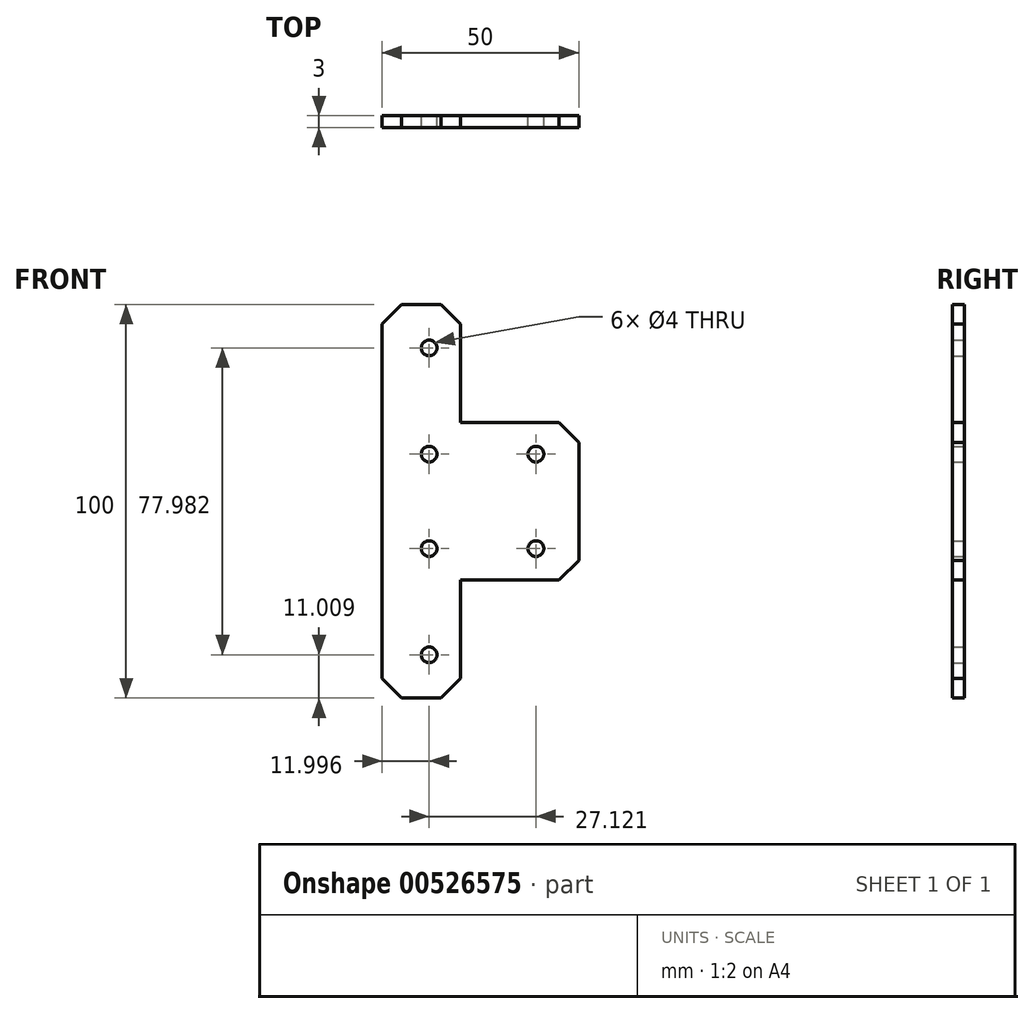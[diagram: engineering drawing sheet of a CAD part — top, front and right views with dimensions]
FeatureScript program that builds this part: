
annotation { "Feature Type Name" : "Feature", "Feature Type Description" : "" }
export const myFeature = defineFeature(function(context is Context, id is Id, definition is map)
    precondition{}
    {
        {
            var Q0;
            Q0=qCreatedBy(makeId("Front.planeOp"),FACE);
            var sketch = newSketch(context, id + "F0", { "sketchPlane" : qUnion([Q0])});
            skLineSegment(sketch, "E0", {"start": v(-55.77, 50) * mm, "end": v(-55.77, 0) * mm});
            skLineSegment(sketch, "E1", {"start": v(-55.77, 0) * mm, "end": v(-5.77, 0) * mm});
            skLineSegment(sketch, "E2", {"start": v(-5.77, 0) * mm, "end": v(-5.77, 20) * mm});
            skLineSegment(sketch, "E3", {"start": v(-5.77, 20) * mm, "end": v(-35.77, 20) * mm});
            skLineSegment(sketch, "E4", {"start": v(-35.77, 20) * mm, "end": v(-35.77, 50) * mm});
            skLineSegment(sketch, "E5", {"start": v(-35.77, 50) * mm, "end": v(-55.77, 50) * mm});
            skCircle(sketch, "E6", {"center": v(-43.77, 39) * mm, "radius": 2 * mm});
            skPoint(sketch, "E6.centerSnap0", {"position": v(-45.77, 50) * mm});
            skCircle(sketch, "E7", {"center": v(-16.65, 12) * mm, "radius": 2 * mm});
            skPoint(sketch, "E7.centerSnap0", {"position": v(-5.77, 10) * mm});
            skCircle(sketch, "E8", {"center": v(-43.77, 12) * mm, "radius": 2 * mm});
            skSolve(sketch);
        }
        {
            var Q0;
            Q0 = qSketchRegion(id + "F0", true);
            extrude(context, id + "F1", {"entities" : qUnion([Q0]), "depth" : 3 * mm, "offsetDistance" : 25 * mm});
        }
        {
            var Q0;
            Q0=makeQuery(id+"F1.opExtrude","SWEPT_BODY",BODY,{"disambiguationData":[OSD([sQuery(id+"F0.wireOp",EDGE,"E0"),sQuery(id+"F0.wireOp",EDGE,"E1"),sQuery(id+"F0.wireOp",EDGE,"E2"),sQuery(id+"F0.wireOp",EDGE,"E3"),sQuery(id+"F0.wireOp",EDGE,"E4"),sQuery(id+"F0.wireOp",EDGE,"E5"),sQuery(id+"F0.wireOp",EDGE,"E6"),sQuery(id+"F0.wireOp",EDGE,"E7"),sQuery(id+"F0.wireOp",EDGE,"E8")])]});
            var Q1;
            Q1=makeQuery(id+"F1.opExtrude","SWEPT_FACE",FACE,{"disambiguationData":[OSD([sQuery(id+"F0.wireOp",EDGE,"E1")])]});
            mirror(context, id + "F2", {"operationType" : NewBodyOperationType.ADD, "entities" : qUnion([Q0]), "mirrorPlane" : qUnion([Q1])});
        }
        {
            var Q0;
            Q0=makeQuery(id+"F1.opExtrude","SWEPT_EDGE",EDGE,{"disambiguationData":[OSD([sQuery(id+"F0.wireOp",EDGE,"E2"),sQuery(id+"F0.wireOp",EDGE,"E3")])]});
            var Q1;
            Q1=makeQuery(id+"F2.opPattern","COPY",EDGE,{"derivedFrom":makeQuery(id+"F1.opExtrude","SWEPT_EDGE",EDGE,{"disambiguationData":[OSD([sQuery(id+"F0.wireOp",EDGE,"E2"),sQuery(id+"F0.wireOp",EDGE,"E3")])]}),"instanceName":"1"});
            var Q2;
            Q2=makeQuery(id+"F1.opExtrude","SWEPT_EDGE",EDGE,{"disambiguationData":[OSD([sQuery(id+"F0.wireOp",EDGE,"E4"),sQuery(id+"F0.wireOp",EDGE,"E5")])]});
            var Q3;
            Q3=makeQuery(id+"F2.opPattern","COPY",EDGE,{"derivedFrom":makeQuery(id+"F1.opExtrude","SWEPT_EDGE",EDGE,{"disambiguationData":[OSD([sQuery(id+"F0.wireOp",EDGE,"E4"),sQuery(id+"F0.wireOp",EDGE,"E5")])]}),"instanceName":"1"});
            var Q4;
            Q4=makeQuery(id+"F1.opExtrude","SWEPT_EDGE",EDGE,{"disambiguationData":[OSD([sQuery(id+"F0.wireOp",EDGE,"E0"),sQuery(id+"F0.wireOp",EDGE,"E5")])]});
            var Q5;
            Q5=makeQuery(id+"F2.opPattern","COPY",EDGE,{"derivedFrom":makeQuery(id+"F1.opExtrude","SWEPT_EDGE",EDGE,{"disambiguationData":[OSD([sQuery(id+"F0.wireOp",EDGE,"E0"),sQuery(id+"F0.wireOp",EDGE,"E5")])]}),"instanceName":"1"});
            chamfer(context, id + "F3", {"entities" : qUnion([Q0, Q1, Q2, Q3, Q4, Q5]), "width" : 5 * mm, "tangentPropagation" : true});
        }
    });
